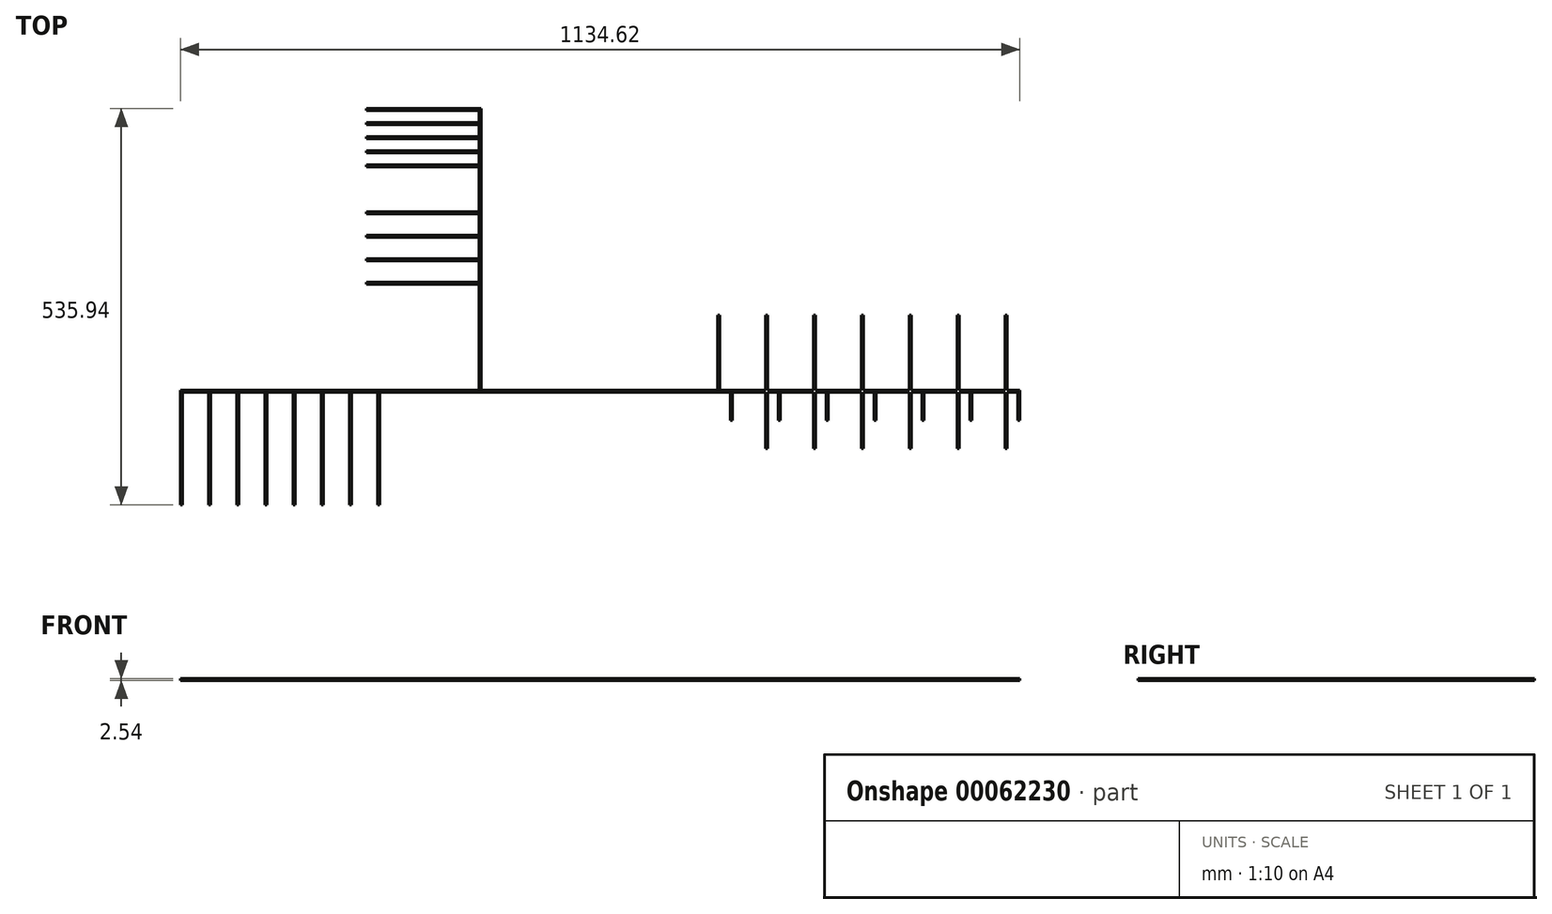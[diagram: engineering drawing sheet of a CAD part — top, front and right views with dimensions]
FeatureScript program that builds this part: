
annotation { "Feature Type Name" : "Feature", "Feature Type Description" : "" }
export const myFeature = defineFeature(function(context is Context, id is Id, definition is map)
    precondition{}
    {
        {
            var Q0;
            Q0=qCreatedBy(makeId("Top.planeOp"),FACE);
            var sketch = newSketch(context, id + "F0", { "sketchPlane" : qUnion([Q0])});
            skLineSegment(sketch, "E0.bottom", {"start": v(203.2, 1.27) * mm, "end": v(-203.2, 1.27) * mm});
            skLineSegment(sketch, "E0.top", {"start": v(203.2, -1.27) * mm, "end": v(-203.2, -1.27) * mm});
            skLineSegment(sketch, "E0.left", {"start": v(203.2, 1.27) * mm, "end": v(203.2, -1.27) * mm});
            skLineSegment(sketch, "E0.right", {"start": v(-203.2, 1.27) * mm, "end": v(-203.2, -1.27) * mm});
            skPoint(sketch, "E0.middle", {"position": v(0, 0) * mm});
            skLineSegment(sketch, "E1.bottom", {"start": v(-203.2, 1.27) * mm, "end": v(-508, 1.27) * mm});
            skLineSegment(sketch, "E1.top", {"start": v(-203.2, -1.27) * mm, "end": v(-508, -1.27) * mm});
            skLineSegment(sketch, "E1.right", {"start": v(-508, 1.27) * mm, "end": v(-508, -1.27) * mm});
            skLineSegment(sketch, "E2.bottom", {"start": v(-508, 1.27) * mm, "end": v(-914.4, 1.27) * mm});
            skLineSegment(sketch, "E2.top", {"start": v(-508, -1.27) * mm, "end": v(-914.4, -1.27) * mm});
            skLineSegment(sketch, "E2.right", {"start": v(-914.4, 1.27) * mm, "end": v(-914.4, -1.27) * mm});
            skLineSegment(sketch, "E3.bottom", {"start": v(-508, 1.27) * mm, "end": v(-510.54, 1.27) * mm});
            skLineSegment(sketch, "E3.top", {"start": v(-508, 382.27) * mm, "end": v(-510.54, 382.27) * mm});
            skLineSegment(sketch, "E3.left", {"start": v(-508, 1.27) * mm, "end": v(-508, 382.27) * mm});
            skLineSegment(sketch, "E3.right", {"start": v(-510.54, 1.27) * mm, "end": v(-510.54, 382.27) * mm});
            skLineSegment(sketch, "E4.bottom", {"start": v(-510.54, 382.27) * mm, "end": v(-662.94, 382.27) * mm});
            skLineSegment(sketch, "E4.top", {"start": v(-510.54, 379.73) * mm, "end": v(-662.94, 379.73) * mm});
            skLineSegment(sketch, "E4.left", {"start": v(-510.54, 382.27) * mm, "end": v(-510.54, 379.73) * mm});
            skLineSegment(sketch, "E4.right", {"start": v(-662.94, 382.27) * mm, "end": v(-662.94, 379.73) * mm});
            skLineSegment(sketch, "E5.bottom", {"start": v(-510.54, 363.22) * mm, "end": v(-662.94, 363.22) * mm});
            skLineSegment(sketch, "E5.top", {"start": v(-510.54, 360.68) * mm, "end": v(-662.94, 360.68) * mm});
            skLineSegment(sketch, "E5.left", {"start": v(-510.54, 363.22) * mm, "end": v(-510.54, 360.68) * mm});
            skLineSegment(sketch, "E5.right", {"start": v(-662.94, 363.22) * mm, "end": v(-662.94, 360.68) * mm});
            skLineSegment(sketch, "E6.bottom", {"start": v(-510.54, 344.17) * mm, "end": v(-662.94, 344.17) * mm});
            skLineSegment(sketch, "E6.top", {"start": v(-510.54, 341.63) * mm, "end": v(-662.94, 341.63) * mm});
            skLineSegment(sketch, "E6.left", {"start": v(-510.54, 344.17) * mm, "end": v(-510.54, 341.63) * mm});
            skLineSegment(sketch, "E6.right", {"start": v(-662.94, 344.17) * mm, "end": v(-662.94, 341.63) * mm});
            skLineSegment(sketch, "E7.bottom", {"start": v(-510.54, 325.12) * mm, "end": v(-662.94, 325.12) * mm});
            skLineSegment(sketch, "E7.top", {"start": v(-510.54, 322.58) * mm, "end": v(-662.94, 322.58) * mm});
            skLineSegment(sketch, "E7.left", {"start": v(-510.54, 325.12) * mm, "end": v(-510.54, 322.58) * mm});
            skLineSegment(sketch, "E7.right", {"start": v(-662.94, 325.12) * mm, "end": v(-662.94, 322.58) * mm});
            skLineSegment(sketch, "E8.bottom", {"start": v(-510.54, 306.07) * mm, "end": v(-662.94, 306.07) * mm});
            skLineSegment(sketch, "E8.top", {"start": v(-510.54, 303.53) * mm, "end": v(-662.94, 303.53) * mm});
            skLineSegment(sketch, "E8.left", {"start": v(-510.54, 306.07) * mm, "end": v(-510.54, 303.53) * mm});
            skLineSegment(sketch, "E8.right", {"start": v(-662.94, 306.07) * mm, "end": v(-662.94, 303.53) * mm});
            skLineSegment(sketch, "E9.bottom", {"start": v(-510.54, 242.57) * mm, "end": v(-662.94, 242.57) * mm});
            skLineSegment(sketch, "E9.top", {"start": v(-510.54, 240.03) * mm, "end": v(-662.94, 240.03) * mm});
            skLineSegment(sketch, "E9.left", {"start": v(-510.54, 242.57) * mm, "end": v(-510.54, 240.03) * mm});
            skLineSegment(sketch, "E9.right", {"start": v(-662.94, 242.57) * mm, "end": v(-662.94, 240.03) * mm});
            skLineSegment(sketch, "E10.bottom", {"start": v(-510.54, 210.82) * mm, "end": v(-662.94, 210.82) * mm});
            skLineSegment(sketch, "E10.top", {"start": v(-510.54, 208.28) * mm, "end": v(-662.94, 208.28) * mm});
            skLineSegment(sketch, "E10.left", {"start": v(-510.54, 210.82) * mm, "end": v(-510.54, 208.28) * mm});
            skLineSegment(sketch, "E10.right", {"start": v(-662.94, 210.82) * mm, "end": v(-662.94, 208.28) * mm});
            skLineSegment(sketch, "E11.bottom", {"start": v(-510.54, 179.07) * mm, "end": v(-662.94, 179.07) * mm});
            skLineSegment(sketch, "E11.top", {"start": v(-510.54, 176.53) * mm, "end": v(-662.94, 176.53) * mm});
            skLineSegment(sketch, "E11.left", {"start": v(-510.54, 179.07) * mm, "end": v(-510.54, 176.53) * mm});
            skLineSegment(sketch, "E11.right", {"start": v(-662.94, 179.07) * mm, "end": v(-662.94, 176.53) * mm});
            skLineSegment(sketch, "E12.bottom", {"start": v(-510.54, 147.32) * mm, "end": v(-662.94, 147.32) * mm});
            skLineSegment(sketch, "E12.top", {"start": v(-510.54, 144.78) * mm, "end": v(-662.94, 144.78) * mm});
            skLineSegment(sketch, "E12.left", {"start": v(-510.54, 147.32) * mm, "end": v(-510.54, 144.78) * mm});
            skLineSegment(sketch, "E12.right", {"start": v(-662.94, 147.32) * mm, "end": v(-662.94, 144.78) * mm});
            skLineSegment(sketch, "E13.bottom", {"start": v(-914.4, -1.27) * mm, "end": v(-911.86, -1.27) * mm});
            skLineSegment(sketch, "E13.top", {"start": v(-914.4, -153.67) * mm, "end": v(-911.86, -153.67) * mm});
            skLineSegment(sketch, "E13.left", {"start": v(-914.4, -1.27) * mm, "end": v(-914.4, -153.67) * mm});
            skLineSegment(sketch, "E13.right", {"start": v(-911.86, -1.27) * mm, "end": v(-911.86, -153.67) * mm});
            skLineSegment(sketch, "E14.bottom", {"start": v(-876.3, -1.27) * mm, "end": v(-873.76, -1.27) * mm});
            skLineSegment(sketch, "E14.top", {"start": v(-876.3, -153.67) * mm, "end": v(-873.76, -153.67) * mm});
            skLineSegment(sketch, "E14.left", {"start": v(-876.3, -1.27) * mm, "end": v(-876.3, -153.67) * mm});
            skLineSegment(sketch, "E14.right", {"start": v(-873.76, -1.27) * mm, "end": v(-873.76, -153.67) * mm});
            skLineSegment(sketch, "E15.bottom", {"start": v(-838.2, -1.27) * mm, "end": v(-835.66, -1.27) * mm});
            skLineSegment(sketch, "E15.top", {"start": v(-838.2, -153.67) * mm, "end": v(-835.66, -153.67) * mm});
            skLineSegment(sketch, "E15.left", {"start": v(-838.2, -1.27) * mm, "end": v(-838.2, -153.67) * mm});
            skLineSegment(sketch, "E15.right", {"start": v(-835.66, -1.27) * mm, "end": v(-835.66, -153.67) * mm});
            skLineSegment(sketch, "E16.bottom", {"start": v(-800.1, -1.27) * mm, "end": v(-797.56, -1.27) * mm});
            skLineSegment(sketch, "E16.top", {"start": v(-800.1, -153.67) * mm, "end": v(-797.56, -153.67) * mm});
            skLineSegment(sketch, "E16.left", {"start": v(-800.1, -1.27) * mm, "end": v(-800.1, -153.67) * mm});
            skLineSegment(sketch, "E16.right", {"start": v(-797.56, -1.27) * mm, "end": v(-797.56, -153.67) * mm});
            skLineSegment(sketch, "E17.bottom", {"start": v(-762, -1.27) * mm, "end": v(-759.46, -1.27) * mm});
            skLineSegment(sketch, "E17.top", {"start": v(-762, -153.67) * mm, "end": v(-759.46, -153.67) * mm});
            skLineSegment(sketch, "E17.left", {"start": v(-762, -1.27) * mm, "end": v(-762, -153.67) * mm});
            skLineSegment(sketch, "E17.right", {"start": v(-759.46, -1.27) * mm, "end": v(-759.46, -153.67) * mm});
            skLineSegment(sketch, "E18.bottom", {"start": v(-723.9, -1.27) * mm, "end": v(-721.36, -1.27) * mm});
            skLineSegment(sketch, "E18.top", {"start": v(-723.9, -153.67) * mm, "end": v(-721.36, -153.67) * mm});
            skLineSegment(sketch, "E18.left", {"start": v(-723.9, -1.27) * mm, "end": v(-723.9, -153.67) * mm});
            skLineSegment(sketch, "E18.right", {"start": v(-721.36, -1.27) * mm, "end": v(-721.36, -153.67) * mm});
            skLineSegment(sketch, "E19.bottom", {"start": v(-685.8, -1.27) * mm, "end": v(-683.26, -1.27) * mm});
            skLineSegment(sketch, "E19.top", {"start": v(-685.8, -153.67) * mm, "end": v(-683.26, -153.67) * mm});
            skLineSegment(sketch, "E19.left", {"start": v(-685.8, -1.27) * mm, "end": v(-685.8, -153.67) * mm});
            skLineSegment(sketch, "E19.right", {"start": v(-683.26, -1.27) * mm, "end": v(-683.26, -153.67) * mm});
            skLineSegment(sketch, "E20.bottom", {"start": v(-647.7, -1.27) * mm, "end": v(-645.16, -1.27) * mm});
            skLineSegment(sketch, "E20.top", {"start": v(-647.7, -153.67) * mm, "end": v(-645.16, -153.67) * mm});
            skLineSegment(sketch, "E20.left", {"start": v(-647.7, -1.27) * mm, "end": v(-647.7, -153.67) * mm});
            skLineSegment(sketch, "E20.right", {"start": v(-645.16, -1.27) * mm, "end": v(-645.16, -153.67) * mm});
            skLineSegment(sketch, "E21.bottom", {"start": v(203.2, 1.27) * mm, "end": v(200.66, 1.27) * mm});
            skLineSegment(sketch, "E21.top", {"start": v(203.2, 102.87) * mm, "end": v(200.66, 102.87) * mm});
            skLineSegment(sketch, "E21.left", {"start": v(203.2, 1.27) * mm, "end": v(203.2, 102.87) * mm});
            skLineSegment(sketch, "E21.right", {"start": v(200.66, 1.27) * mm, "end": v(200.66, 102.87) * mm});
            skLineSegment(sketch, "E22.bottom", {"start": v(138.43, 1.27) * mm, "end": v(135.9, 1.27) * mm});
            skLineSegment(sketch, "E22.top", {"start": v(138.43, 102.87) * mm, "end": v(135.9, 102.87) * mm});
            skLineSegment(sketch, "E22.left", {"start": v(138.43, 1.27) * mm, "end": v(138.43, 102.87) * mm});
            skLineSegment(sketch, "E22.right", {"start": v(135.9, 1.27) * mm, "end": v(135.9, 102.87) * mm});
            skLineSegment(sketch, "E23.bottom", {"start": v(73.66, 1.27) * mm, "end": v(71.12, 1.27) * mm});
            skLineSegment(sketch, "E23.top", {"start": v(73.66, 102.87) * mm, "end": v(71.12, 102.87) * mm});
            skLineSegment(sketch, "E23.left", {"start": v(73.66, 1.27) * mm, "end": v(73.66, 102.87) * mm});
            skLineSegment(sketch, "E23.right", {"start": v(71.12, 1.27) * mm, "end": v(71.12, 102.87) * mm});
            skLineSegment(sketch, "E24.bottom", {"start": v(8.89, 1.27) * mm, "end": v(6.35, 1.27) * mm});
            skLineSegment(sketch, "E24.top", {"start": v(8.89, 102.87) * mm, "end": v(6.35, 102.87) * mm});
            skLineSegment(sketch, "E24.left", {"start": v(8.89, 1.27) * mm, "end": v(8.89, 102.87) * mm});
            skLineSegment(sketch, "E24.right", {"start": v(6.35, 1.27) * mm, "end": v(6.35, 102.87) * mm});
            skLineSegment(sketch, "E25.bottom", {"start": v(-55.88, 1.27) * mm, "end": v(-58.42, 1.27) * mm});
            skLineSegment(sketch, "E25.top", {"start": v(-55.88, 102.87) * mm, "end": v(-58.42, 102.87) * mm});
            skLineSegment(sketch, "E25.left", {"start": v(-55.88, 1.27) * mm, "end": v(-55.88, 102.87) * mm});
            skLineSegment(sketch, "E25.right", {"start": v(-58.42, 1.27) * mm, "end": v(-58.42, 102.87) * mm});
            skLineSegment(sketch, "E26.bottom", {"start": v(-123.2, 1.27) * mm, "end": v(-120.65, 1.27) * mm});
            skLineSegment(sketch, "E26.top", {"start": v(-123.2, 102.87) * mm, "end": v(-120.65, 102.87) * mm});
            skLineSegment(sketch, "E26.left", {"start": v(-123.2, 1.27) * mm, "end": v(-123.2, 102.87) * mm});
            skLineSegment(sketch, "E26.right", {"start": v(-120.65, 1.27) * mm, "end": v(-120.65, 102.87) * mm});
            skLineSegment(sketch, "E27.bottom", {"start": v(-185.42, 1.27) * mm, "end": v(-187.96, 1.27) * mm});
            skLineSegment(sketch, "E27.top", {"start": v(-185.42, 102.87) * mm, "end": v(-187.96, 102.87) * mm});
            skLineSegment(sketch, "E27.left", {"start": v(-185.42, 1.27) * mm, "end": v(-185.42, 102.87) * mm});
            skLineSegment(sketch, "E27.right", {"start": v(-187.96, 1.27) * mm, "end": v(-187.96, 102.87) * mm});
            skLineSegment(sketch, "E28.bottom", {"start": v(138.43, -1.27) * mm, "end": v(135.9, -1.27) * mm});
            skLineSegment(sketch, "E28.top", {"start": v(138.43, -77.47) * mm, "end": v(135.9, -77.47) * mm});
            skLineSegment(sketch, "E28.left", {"start": v(138.43, -1.27) * mm, "end": v(138.43, -77.47) * mm});
            skLineSegment(sketch, "E28.right", {"start": v(135.9, -1.27) * mm, "end": v(135.9, -77.47) * mm});
            skLineSegment(sketch, "E29.bottom", {"start": v(73.66, -1.27) * mm, "end": v(71.12, -1.27) * mm});
            skLineSegment(sketch, "E29.top", {"start": v(73.66, -77.47) * mm, "end": v(71.12, -77.47) * mm});
            skLineSegment(sketch, "E29.left", {"start": v(73.66, -1.27) * mm, "end": v(73.66, -77.47) * mm});
            skLineSegment(sketch, "E29.right", {"start": v(71.12, -1.27) * mm, "end": v(71.12, -77.47) * mm});
            skLineSegment(sketch, "E30.bottom", {"start": v(8.89, -1.27) * mm, "end": v(6.35, -1.27) * mm});
            skLineSegment(sketch, "E30.top", {"start": v(8.9, -77.47) * mm, "end": v(6.35, -77.47) * mm});
            skLineSegment(sketch, "E30.left", {"start": v(8.89, -1.27) * mm, "end": v(8.89, -77.47) * mm});
            skLineSegment(sketch, "E30.right", {"start": v(6.35, -1.27) * mm, "end": v(6.35, -77.47) * mm});
            skLineSegment(sketch, "E31.bottom", {"start": v(-55.88, -1.27) * mm, "end": v(-58.42, -1.27) * mm});
            skLineSegment(sketch, "E31.top", {"start": v(-55.88, -77.47) * mm, "end": v(-58.42, -77.47) * mm});
            skLineSegment(sketch, "E31.left", {"start": v(-55.88, -1.27) * mm, "end": v(-55.88, -77.47) * mm});
            skLineSegment(sketch, "E31.right", {"start": v(-58.42, -1.27) * mm, "end": v(-58.42, -77.47) * mm});
            skLineSegment(sketch, "E32.bottom", {"start": v(-120.65, -1.27) * mm, "end": v(-123.2, -1.27) * mm});
            skLineSegment(sketch, "E32.top", {"start": v(-120.65, -77.47) * mm, "end": v(-123.2, -77.47) * mm});
            skLineSegment(sketch, "E32.left", {"start": v(-120.65, -1.27) * mm, "end": v(-120.65, -77.47) * mm});
            skLineSegment(sketch, "E32.right", {"start": v(-123.2, -1.27) * mm, "end": v(-123.2, -77.47) * mm});
            skLineSegment(sketch, "E33.bottom", {"start": v(-185.42, -1.27) * mm, "end": v(-187.96, -1.27) * mm});
            skLineSegment(sketch, "E34.bottom", {"start": v(220.22, -1.27) * mm, "end": v(217.68, -1.27) * mm});
            skLineSegment(sketch, "E34.top", {"start": v(220.22, -39.37) * mm, "end": v(217.68, -39.37) * mm});
            skLineSegment(sketch, "E34.left", {"start": v(220.22, -1.27) * mm, "end": v(220.22, -39.37) * mm});
            skLineSegment(sketch, "E34.right", {"start": v(217.68, -1.27) * mm, "end": v(217.68, -39.37) * mm});
            skLineSegment(sketch, "E35.bottom", {"start": v(155.45, -1.27) * mm, "end": v(152.9, -1.27) * mm});
            skLineSegment(sketch, "E35.top", {"start": v(155.45, -39.37) * mm, "end": v(152.9, -39.37) * mm});
            skLineSegment(sketch, "E35.left", {"start": v(155.45, -1.27) * mm, "end": v(155.45, -39.37) * mm});
            skLineSegment(sketch, "E35.right", {"start": v(152.9, -1.27) * mm, "end": v(152.9, -39.37) * mm});
            skLineSegment(sketch, "E36.bottom", {"start": v(90.68, -1.27) * mm, "end": v(88.14, -1.27) * mm});
            skLineSegment(sketch, "E36.top", {"start": v(90.68, -39.37) * mm, "end": v(88.14, -39.37) * mm});
            skLineSegment(sketch, "E36.left", {"start": v(90.68, -1.27) * mm, "end": v(90.68, -39.37) * mm});
            skLineSegment(sketch, "E36.right", {"start": v(88.14, -1.27) * mm, "end": v(88.14, -39.37) * mm});
            skLineSegment(sketch, "E37.bottom", {"start": v(25.9, -1.27) * mm, "end": v(23.37, -1.27) * mm});
            skLineSegment(sketch, "E37.top", {"start": v(25.9, -39.37) * mm, "end": v(23.37, -39.37) * mm});
            skLineSegment(sketch, "E37.left", {"start": v(25.9, -1.27) * mm, "end": v(25.9, -39.37) * mm});
            skLineSegment(sketch, "E37.right", {"start": v(23.37, -1.27) * mm, "end": v(23.37, -39.37) * mm});
            skLineSegment(sketch, "E38.bottom", {"start": v(-38.86, -1.27) * mm, "end": v(-41.4, -1.27) * mm});
            skLineSegment(sketch, "E38.top", {"start": v(-38.86, -39.37) * mm, "end": v(-41.4, -39.37) * mm});
            skLineSegment(sketch, "E38.left", {"start": v(-38.86, -1.27) * mm, "end": v(-38.86, -39.37) * mm});
            skLineSegment(sketch, "E38.right", {"start": v(-41.4, -1.27) * mm, "end": v(-41.4, -39.37) * mm});
            skLineSegment(sketch, "E39.bottom", {"start": v(-103.63, -1.27) * mm, "end": v(-106.17, -1.27) * mm});
            skLineSegment(sketch, "E39.top", {"start": v(-103.63, -39.37) * mm, "end": v(-106.17, -39.37) * mm});
            skLineSegment(sketch, "E39.left", {"start": v(-103.63, -1.27) * mm, "end": v(-103.63, -39.37) * mm});
            skLineSegment(sketch, "E39.right", {"start": v(-106.17, -1.27) * mm, "end": v(-106.17, -39.37) * mm});
            skLineSegment(sketch, "E40.bottom", {"start": v(-168.4, -1.27) * mm, "end": v(-170.94, -1.27) * mm});
            skLineSegment(sketch, "E40.top", {"start": v(-168.4, -39.37) * mm, "end": v(-170.94, -39.37) * mm});
            skLineSegment(sketch, "E40.left", {"start": v(-168.4, -1.27) * mm, "end": v(-168.4, -39.37) * mm});
            skLineSegment(sketch, "E40.right", {"start": v(-170.94, -1.27) * mm, "end": v(-170.94, -39.37) * mm});
            skLineSegment(sketch, "E41.bottom", {"start": v(203.2, 1.27) * mm, "end": v(220.22, 1.27) * mm});
            skLineSegment(sketch, "E41.top", {"start": v(203.2, -1.27) * mm, "end": v(220.22, -1.27) * mm});
            skLineSegment(sketch, "E41.right", {"start": v(220.22, 1.27) * mm, "end": v(220.22, -1.27) * mm});
            skLineSegment(sketch, "E42.bottom", {"start": v(203.2, -1.27) * mm, "end": v(200.66, -1.27) * mm});
            skLineSegment(sketch, "E42.top", {"start": v(203.2, -77.47) * mm, "end": v(200.66, -77.47) * mm});
            skLineSegment(sketch, "E42.left", {"start": v(203.2, -1.27) * mm, "end": v(203.2, -77.47) * mm});
            skLineSegment(sketch, "E42.right", {"start": v(200.66, -1.27) * mm, "end": v(200.66, -77.47) * mm});
            skPoint(sketch, "E43.positionSnap0", {"position": v(7.62, 1.27) * mm});
            skSolve(sketch);
        }
        {
            var Q0;
            Q0 = qSketchRegion(id + "F0", true);
            extrude(context, id + "F1", {"entities" : qUnion([Q0]), "depth" : 2.54 * mm});
        }
    });
